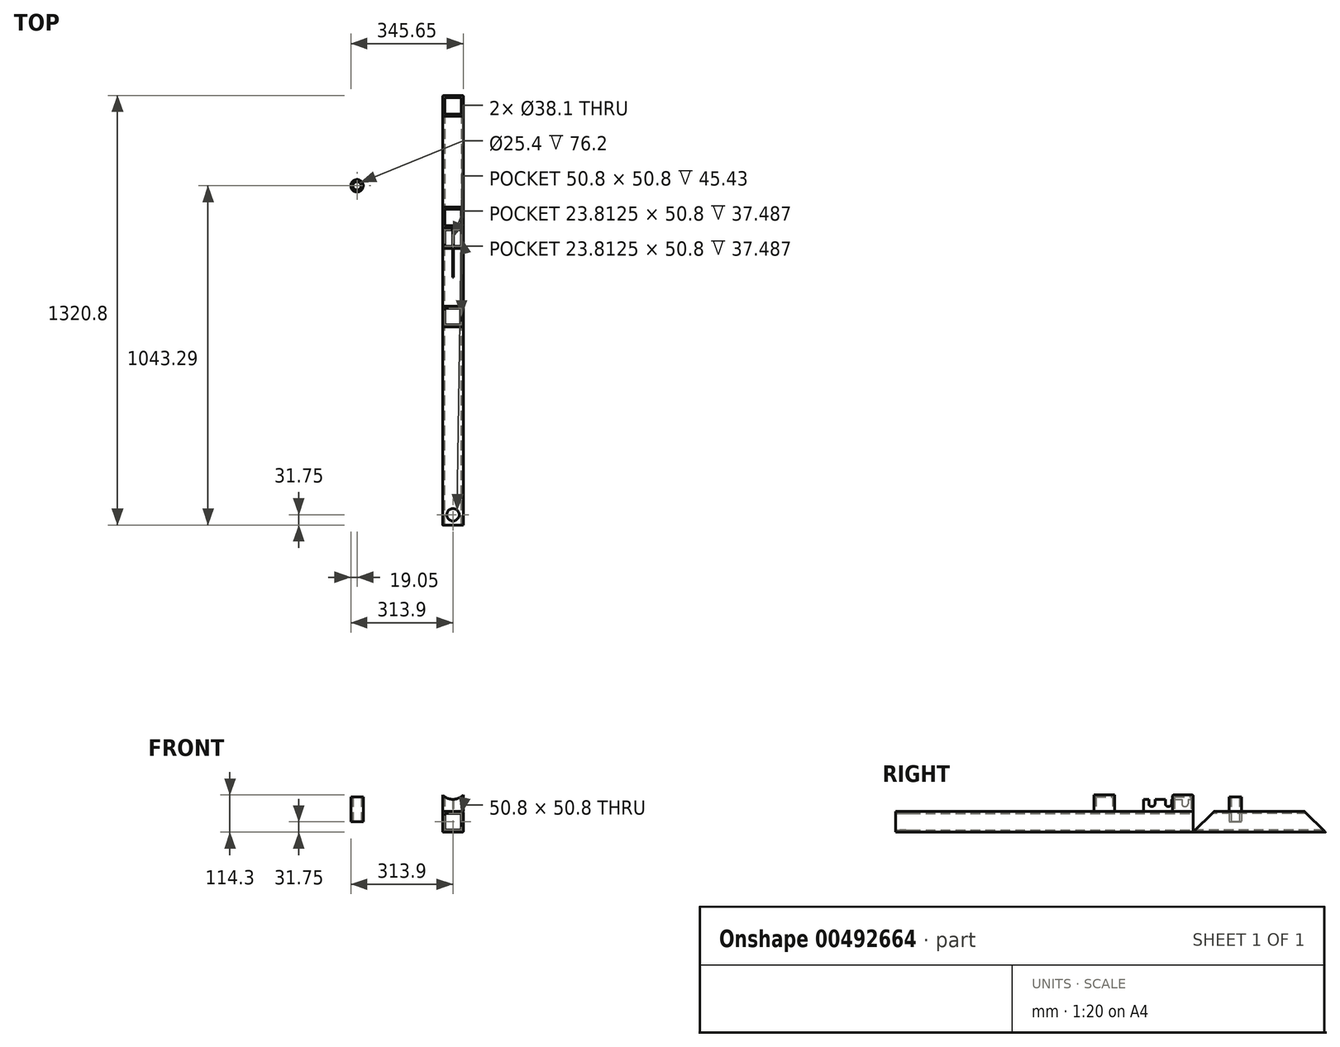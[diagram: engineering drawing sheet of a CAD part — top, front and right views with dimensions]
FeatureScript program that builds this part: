
annotation { "Feature Type Name" : "Feature", "Feature Type Description" : "" }
export const myFeature = defineFeature(function(context is Context, id is Id, definition is map)
    precondition{}
    {
        {
            var Q0;
            Q0=qCreatedBy(makeId("Front.planeOp"),FACE);
            var sketch = newSketch(context, id + "F0", { "sketchPlane" : qUnion([Q0])});
            skLineSegment(sketch, "E0.bottom", {"start": v(28.75, -31.75) * mm, "end": v(-28.75, -31.75) * mm});
            skLineSegment(sketch, "E0.top", {"start": v(28.75, 31.75) * mm, "end": v(-28.75, 31.75) * mm});
            skLineSegment(sketch, "E0.left", {"start": v(31.75, -28.75) * mm, "end": v(31.75, 28.75) * mm});
            skLineSegment(sketch, "E0.right", {"start": v(-31.75, -28.75) * mm, "end": v(-31.75, 28.75) * mm});
            skPoint(sketch, "E0.middle", {"position": v(0, 0) * mm});
            skLineSegment(sketch, "E1.bottom", {"start": v(25.4, -25.4) * mm, "end": v(-25.4, -25.4) * mm});
            skLineSegment(sketch, "E1.top", {"start": v(25.4, 25.4) * mm, "end": v(-25.4, 25.4) * mm});
            skLineSegment(sketch, "E1.left", {"start": v(25.4, -25.4) * mm, "end": v(25.4, 25.4) * mm});
            skLineSegment(sketch, "E1.right", {"start": v(-25.4, -25.4) * mm, "end": v(-25.4, 25.4) * mm});
            skPoint(sketch, "E2.visualSharp", {"position": v(-31.75, 31.75) * mm});
            skArc(sketch, "E2.filletArc", {"start": v(-28.75, 31.75) * mm, "mid": v(-30.87, 30.87) * mm, "end": v(-31.75, 28.75) * mm});
            skPoint(sketch, "E3.visualSharp", {"position": v(31.75, 31.75) * mm});
            skArc(sketch, "E3.filletArc", {"start": v(31.75, 28.75) * mm, "mid": v(30.87, 30.87) * mm, "end": v(28.75, 31.75) * mm});
            skPoint(sketch, "E4.visualSharp", {"position": v(31.75, -31.75) * mm});
            skArc(sketch, "E4.filletArc", {"start": v(28.75, -31.75) * mm, "mid": v(30.87, -30.87) * mm, "end": v(31.75, -28.75) * mm});
            skPoint(sketch, "E5.visualSharp", {"position": v(-31.75, -31.75) * mm});
            skArc(sketch, "E5.filletArc", {"start": v(-31.75, -28.75) * mm, "mid": v(-30.87, -30.87) * mm, "end": v(-28.75, -31.75) * mm});
            skSolve(sketch);
        }
        {
            var Q0;
            Q0 = qSketchRegion(id + "F0", true);
            extrude(context, id + "F1", {"entities" : qUnion([Q0]), "depth" : 609.6 * mm, "offsetDistance" : 25 * mm});
        }
        {
            var Q0;
            Q0 = qSketchRegion(id + "F0", true);
            extrude(context, id + "F2", {"entities" : qUnion([Q0]), "depth" : 304.8 * mm, "offsetDistance" : 25 * mm});
        }
        {
            var Q0;
            Q0 = qSketchRegion(id + "F0", true);
            extrude(context, id + "F3", {"entities" : qUnion([Q0]), "oppositeDirection" : true, "depth" : 406.4 * mm, "offsetDistance" : 25 * mm});
        }
        {
            var Q0;
            Q0=makeQuery(id+"F3.opExtrude","SWEPT_FACE",FACE,{"disambiguationData":[OSD([sQuery(id+"F0.wireOp",EDGE,"E0.right")])]});
            var sketch = newSketch(context, id + "F4", { "sketchPlane" : qUnion([Q0])});
            skPoint(sketch, "E6.middle", {"position": v(-374.65, 0) * mm});
            skPoint(sketch, "E6.middle.positionSnap0", {"position": v(-406.4, 0) * mm});
            skPoint(sketch, "E6.centerSnap0", {"position": v(-406.4, 0) * mm});
            skLineSegment(sketch, "E7", {"start": v(-406.4, -28.75) * mm, "end": v(-406.4, 28.75) * mm});
            skLineSegment(sketch, "E8", {"start": v(-342.9, 31.75) * mm, "end": v(-406.4, 31.75) * mm});
            skLineSegment(sketch, "E9", {"start": v(-342.9, 31.75) * mm, "end": v(-406.4, -31.75) * mm});
            skLineSegment(sketch, "E10", {"start": v(-406.4, 31.75) * mm, "end": v(-406.4, -31.75) * mm});
            skSolve(sketch);
        }
        {
            var Q0;
            Q0 = qSketchRegion(id + "F4", true);
            extrude(context, id + "F5", {"entities" : qUnion([Q0]), "operationType" : NewBodyOperationType.REMOVE, "endBound" : BoundingType.THROUGH_ALL, "oppositeDirection" : true, "depth" : 25 * mm, "offsetDistance" : 25 * mm});
        }
        {
            var Q0;
            Q0=makeQuery(id+"F3.opExtrude","SWEPT_FACE",FACE,{"disambiguationData":[OSD([sQuery(id+"F0.wireOp",EDGE,"E0.right")])]});
            var sketch = newSketch(context, id + "F6", { "sketchPlane" : qUnion([Q0])});
            skPoint(sketch, "E11.middle", {"position": v(-31.75, 0) * mm});
            skLineSegment(sketch, "E12", {"start": v(-63.5, 31.75) * mm, "end": v(0, -31.75) * mm});
            skLineSegment(sketch, "E13", {"start": v(0, 31.75) * mm, "end": v(0, -31.75) * mm});
            skLineSegment(sketch, "E14", {"start": v(0, 31.75) * mm, "end": v(-63.5, 31.75) * mm});
            skSolve(sketch);
        }
        {
            var Q0;
            Q0 = qSketchRegion(id + "F6", true);
            extrude(context, id + "F7", {"entities" : qUnion([Q0]), "operationType" : NewBodyOperationType.REMOVE, "endBound" : BoundingType.THROUGH_ALL, "oppositeDirection" : true, "depth" : 25 * mm, "offsetDistance" : 25 * mm});
        }
        {
            var Q0;
            Q0=makeQuery(id+"F1.opExtrude","SWEPT_FACE",FACE,{"disambiguationData":[OSD([sQuery(id+"F0.wireOp",EDGE,"E0.top")])]});
            var sketch = newSketch(context, id + "F8", { "sketchPlane" : qUnion([Q0])});
            skPoint(sketch, "E15.centerSnap0", {"position": v(0, -609.6) * mm});
            skCircle(sketch, "E16", {"center": v(0, -577.85) * mm, "radius": 19.05 * mm});
            skSolve(sketch);
        }
        {
            var Q0;
            Q0 = qSketchRegion(id + "F8", true);
            extrude(context, id + "F9", {"entities" : qUnion([Q0]), "operationType" : NewBodyOperationType.REMOVE, "endBound" : BoundingType.THROUGH_ALL, "oppositeDirection" : true, "depth" : 25.4 * mm, "offsetDistance" : 25 * mm});
        }
        {
            var Q0;
            Q0=qCreatedBy(makeId("Front.planeOp"),FACE);
            var sketch = newSketch(context, id + "F10", { "sketchPlane" : qUnion([Q0])});
            skLineSegment(sketch, "E17.bottom", {"start": v(-25.4, -25.4) * mm, "end": v(25.4, -25.4) * mm});
            skLineSegment(sketch, "E17.top", {"start": v(-25.4, 25.4) * mm, "end": v(25.4, 25.4) * mm});
            skLineSegment(sketch, "E17.left", {"start": v(-25.4, -25.4) * mm, "end": v(-25.4, 25.4) * mm});
            skLineSegment(sketch, "E17.right", {"start": v(25.4, -25.4) * mm, "end": v(25.4, 25.4) * mm});
            skPoint(sketch, "E17.middle", {"position": v(0, 0) * mm});
            skLineSegment(sketch, "E18.bottom", {"start": v(-28.75, -31.75) * mm, "end": v(28.75, -31.75) * mm});
            skLineSegment(sketch, "E18.top", {"start": v(-28.75, 31.75) * mm, "end": v(28.75, 31.75) * mm});
            skLineSegment(sketch, "E18.left", {"start": v(-31.75, -28.75) * mm, "end": v(-31.75, 28.75) * mm});
            skLineSegment(sketch, "E18.right", {"start": v(31.75, -28.75) * mm, "end": v(31.75, 28.75) * mm});
            skPoint(sketch, "E19.visualSharp", {"position": v(31.75, 31.75) * mm});
            skArc(sketch, "E19.filletArc", {"start": v(31.75, 28.75) * mm, "mid": v(30.87, 30.87) * mm, "end": v(28.75, 31.75) * mm});
            skPoint(sketch, "E20.visualSharp", {"position": v(-31.75, 31.75) * mm});
            skArc(sketch, "E20.filletArc", {"start": v(-28.75, 31.75) * mm, "mid": v(-30.87, 30.87) * mm, "end": v(-31.75, 28.75) * mm});
            skPoint(sketch, "E21.visualSharp", {"position": v(-31.75, -31.75) * mm});
            skArc(sketch, "E21.filletArc", {"start": v(-31.75, -28.75) * mm, "mid": v(-30.87, -30.87) * mm, "end": v(-28.75, -31.75) * mm});
            skPoint(sketch, "E22.visualSharp", {"position": v(31.75, -31.75) * mm});
            skArc(sketch, "E22.filletArc", {"start": v(28.75, -31.75) * mm, "mid": v(30.87, -30.87) * mm, "end": v(31.75, -28.75) * mm});
            skSolve(sketch);
        }
        {
            var Q0;
            Q0 = qSketchRegion(id + "F10", true);
            extrude(context, id + "F11", {"entities" : qUnion([Q0]), "depth" : 914.4 * mm, "offsetDistance" : 25 * mm});
        }
        {
            var Q0;
            Q0=makeQuery(id+"F11.opExtrude","SWEPT_FACE",FACE,{"disambiguationData":[OSD([sQuery(id+"F10.wireOp",EDGE,"E18.bottom")])]});
            var sketch = newSketch(context, id + "F12", { "sketchPlane" : qUnion([Q0])});
            skCircle(sketch, "E23", {"center": v(0, 882.65) * mm, "radius": 19.05 * mm});
            skPoint(sketch, "E23.centerSnap0", {"position": v(0, 914.4) * mm});
            skSolve(sketch);
        }
        {
            var Q0;
            Q0 = qSketchRegion(id + "F12", true);
            extrude(context, id + "F13", {"entities" : qUnion([Q0]), "operationType" : NewBodyOperationType.REMOVE, "endBound" : BoundingType.THROUGH_ALL, "oppositeDirection" : true, "depth" : 25.4 * mm, "offsetDistance" : 25 * mm});
        }
        {
            var Q0;
            Q0=makeQuery(id+"F11.opExtrude","SWEPT_FACE",FACE,{"disambiguationData":[OSD([sQuery(id+"F10.wireOp",EDGE,"E18.top")])]});
            var sketch = newSketch(context, id + "F14", { "sketchPlane" : qUnion([Q0])});
            skLineSegment(sketch, "E24.bottom", {"start": v(-1.59, 0) * mm, "end": v(1.59, 0) * mm});
            skLineSegment(sketch, "E24.top", {"start": v(-1.59, -152.4) * mm, "end": v(1.59, -152.4) * mm});
            skLineSegment(sketch, "E24.left", {"start": v(-1.59, 0) * mm, "end": v(-1.59, -152.4) * mm});
            skLineSegment(sketch, "E24.right", {"start": v(1.59, 0) * mm, "end": v(1.59, -152.4) * mm});
            skPoint(sketch, "E24.middle", {"position": v(0, -76.2) * mm});
            skSolve(sketch);
        }
        {
            var Q0;
            Q0 = qSketchRegion(id + "F14", true);
            extrude(context, id + "F15", {"entities" : qUnion([Q0]), "operationType" : NewBodyOperationType.ADD, "depth" : 76.2 * mm, "offsetDistance" : 25 * mm});
        }
        {
            var Q0;
            Q0=makeQuery(id+"F15.opExtrude","SWEPT_FACE",FACE,{"disambiguationData":[OSD([sQuery(id+"F14.wireOp",EDGE,"E24.right")])]});
            var sketch = newSketch(context, id + "F16", { "sketchPlane" : qUnion([Q0])});
            skLineSegment(sketch, "E25", {"start": v(-152.4, 101.6) * mm, "end": v(0, 101.6) * mm, "construction": true});
            skCircle(sketch, "E26", {"center": v(-127, 85.72) * mm, "radius": 15.88 * mm});
            skLineSegment(sketch, "E27", {"start": v(-76.2, 101.6) * mm, "end": v(-76.2, 52.57) * mm, "construction": true});
            skLineSegment(sketch, "E28.bottom", {"start": v(-136.53, 73.02) * mm, "end": v(-117.48, 73.02) * mm});
            skLineSegment(sketch, "E28.top", {"start": v(-128.53, 47.62) * mm, "end": v(-125.48, 47.62) * mm});
            skLineSegment(sketch, "E28.left", {"start": v(-136.53, 73.02) * mm, "end": v(-136.53, 55.62) * mm});
            skLineSegment(sketch, "E28.right", {"start": v(-117.48, 73.02) * mm, "end": v(-117.48, 55.62) * mm});
            skPoint(sketch, "E28.middle", {"position": v(-127, 60.32) * mm});
            skPoint(sketch, "E29.visualSharp", {"position": v(-136.53, 47.62) * mm});
            skArc(sketch, "E29.filletArc", {"start": v(-136.53, 55.62) * mm, "mid": v(-134.18, 49.97) * mm, "end": v(-128.53, 47.62) * mm});
            skPoint(sketch, "E30.visualSharp", {"position": v(-117.48, 47.62) * mm});
            skArc(sketch, "E30.filletArc", {"start": v(-125.48, 47.62) * mm, "mid": v(-119.82, 49.97) * mm, "end": v(-117.47, 55.62) * mm});
            skCircle(sketch, "E31.1.0.0", {"center": v(-76.2, 85.72) * mm, "radius": 15.88 * mm});
            skLineSegment(sketch, "E31.1.0.1", {"start": v(-66.67, 73.02) * mm, "end": v(-66.67, 55.62) * mm});
            skLineSegment(sketch, "E31.1.0.2", {"start": v(-85.72, 73.02) * mm, "end": v(-85.72, 55.62) * mm});
            skLineSegment(sketch, "E31.1.0.3", {"start": v(-85.72, 73.02) * mm, "end": v(-66.67, 73.02) * mm});
            skArc(sketch, "E31.1.0.4", {"start": v(-74.67, 47.62) * mm, "mid": v(-69.02, 49.97) * mm, "end": v(-66.67, 55.62) * mm});
            skLineSegment(sketch, "E31.1.0.5", {"start": v(-77.72, 47.62) * mm, "end": v(-74.67, 47.62) * mm});
            skArc(sketch, "E31.1.0.6", {"start": v(-85.72, 55.62) * mm, "mid": v(-83.38, 49.97) * mm, "end": v(-77.72, 47.62) * mm});
            skCircle(sketch, "E31.2.0.0", {"center": v(-25.4, 85.72) * mm, "radius": 15.88 * mm});
            skLineSegment(sketch, "E31.2.0.1", {"start": v(-15.87, 73.02) * mm, "end": v(-15.87, 55.62) * mm});
            skLineSegment(sketch, "E31.2.0.2", {"start": v(-34.92, 73.02) * mm, "end": v(-34.92, 55.62) * mm});
            skLineSegment(sketch, "E31.2.0.3", {"start": v(-34.92, 73.02) * mm, "end": v(-15.87, 73.02) * mm});
            skArc(sketch, "E31.2.0.4", {"start": v(-23.87, 47.62) * mm, "mid": v(-18.22, 49.97) * mm, "end": v(-15.87, 55.62) * mm});
            skLineSegment(sketch, "E31.2.0.5", {"start": v(-26.92, 47.62) * mm, "end": v(-23.87, 47.62) * mm});
            skArc(sketch, "E31.2.0.6", {"start": v(-34.92, 55.62) * mm, "mid": v(-32.58, 49.97) * mm, "end": v(-26.92, 47.62) * mm});
            skLineSegment(sketch, "E31.direction1", {"start": v(-127, 85.72) * mm, "end": v(-76.2, 85.72) * mm, "construction": true});
            skSolve(sketch);
        }
        {
            var Q0;
            Q0 = qSketchRegion(id + "F16", true);
            extrude(context, id + "F17", {"entities" : qUnion([Q0]), "operationType" : NewBodyOperationType.REMOVE, "endBound" : BoundingType.THROUGH_ALL, "oppositeDirection" : true, "depth" : 25 * mm, "offsetDistance" : 25 * mm});
        }
        {
            var Q0;
            Q0=makeQuery(id+"F2.opExtrude","SWEPT_FACE",FACE,{"disambiguationData":[OSD([sQuery(id+"F0.wireOp",EDGE,"E0.top")])]});
            var sketch = newSketch(context, id + "F18", { "sketchPlane" : qUnion([Q0])});
            skLineSegment(sketch, "E32.bottom", {"start": v(-28.75, 0) * mm, "end": v(28.75, 0) * mm});
            skLineSegment(sketch, "E32.top", {"start": v(-28.75, -63.5) * mm, "end": v(28.75, -63.5) * mm});
            skLineSegment(sketch, "E32.left", {"start": v(-31.75, -3) * mm, "end": v(-31.75, -60.5) * mm});
            skLineSegment(sketch, "E32.right", {"start": v(31.75, -3) * mm, "end": v(31.75, -60.5) * mm});
            skPoint(sketch, "E32.middle", {"position": v(0, -31.75) * mm});
            skLineSegment(sketch, "E33.bottom", {"start": v(25.4, -57.15) * mm, "end": v(-25.4, -57.15) * mm});
            skLineSegment(sketch, "E33.top", {"start": v(25.4, -6.35) * mm, "end": v(-25.4, -6.35) * mm});
            skLineSegment(sketch, "E33.left", {"start": v(25.4, -57.15) * mm, "end": v(25.4, -6.35) * mm});
            skLineSegment(sketch, "E33.right", {"start": v(-25.4, -57.15) * mm, "end": v(-25.4, -6.35) * mm});
            skLineSegment(sketch, "E34", {"start": v(-28.75, -152.4) * mm, "end": v(28.75, -152.4) * mm, "construction": true});
            skLineSegment(sketch, "E35.MirrorCS", {"start": v(25.4, -298.45) * mm, "end": v(-25.4, -298.45) * mm});
            skLineSegment(sketch, "E36.MirrorCS", {"start": v(-31.75, -304.8) * mm, "end": v(31.75, -304.8) * mm});
            skLineSegment(sketch, "E37.MirrorCS", {"start": v(-31.75, -304.8) * mm, "end": v(-31.75, -241.3) * mm});
            skLineSegment(sketch, "E38.MirrorCS", {"start": v(-25.4, -247.65) * mm, "end": v(-25.4, -298.45) * mm});
            skLineSegment(sketch, "E39.MirrorCS", {"start": v(25.4, -247.65) * mm, "end": v(-25.4, -247.65) * mm});
            skLineSegment(sketch, "E40.MirrorCS", {"start": v(-31.75, -241.3) * mm, "end": v(31.75, -241.3) * mm});
            skLineSegment(sketch, "E41.MirrorCS", {"start": v(25.4, -247.65) * mm, "end": v(25.4, -298.45) * mm});
            skLineSegment(sketch, "E42.MirrorCS", {"start": v(31.75, -304.8) * mm, "end": v(31.75, -241.3) * mm});
            skPoint(sketch, "E43.visualSharp", {"position": v(-31.75, 0) * mm});
            skArc(sketch, "E43.filletArc", {"start": v(-28.75, 0) * mm, "mid": v(-30.87, -0.88) * mm, "end": v(-31.75, -3) * mm});
            skPoint(sketch, "E44.visualSharp", {"position": v(-31.75, -63.5) * mm});
            skArc(sketch, "E44.filletArc", {"start": v(-31.75, -60.5) * mm, "mid": v(-30.87, -62.62) * mm, "end": v(-28.75, -63.5) * mm});
            skPoint(sketch, "E45.visualSharp", {"position": v(31.75, -63.5) * mm});
            skArc(sketch, "E45.filletArc", {"start": v(28.75, -63.5) * mm, "mid": v(30.87, -62.62) * mm, "end": v(31.75, -60.5) * mm});
            skPoint(sketch, "E46.visualSharp", {"position": v(31.75, 0) * mm});
            skArc(sketch, "E46.filletArc", {"start": v(31.75, -3) * mm, "mid": v(30.87, -0.88) * mm, "end": v(28.75, 0) * mm});
            skSolve(sketch);
        }
        {
            var Q0;
            Q0 = qSketchRegion(id + "F18", true);
            extrude(context, id + "F19", {"entities" : qUnion([Q0]), "operationType" : NewBodyOperationType.ADD, "depth" : 50.8 * mm, "offsetDistance" : 25 * mm});
        }
        {
            var Q0;
            Q0=makeQuery(id+"F19.boolean.opBoolean","MERGE",FACE,{"derivedFrom":[makeQuery(id+"F2.opExtrude","CAP_FACE",FACE,{"disambiguationData":[OSD([sQuery(id+"F0.wireOp",EDGE,"E0.bottom"),sQuery(id+"F0.wireOp",EDGE,"E0.top"),sQuery(id+"F0.wireOp",EDGE,"E0.left"),sQuery(id+"F0.wireOp",EDGE,"E0.right"),sQuery(id+"F0.wireOp",EDGE,"E1.bottom"),sQuery(id+"F0.wireOp",EDGE,"E1.top"),sQuery(id+"F0.wireOp",EDGE,"E1.left"),sQuery(id+"F0.wireOp",EDGE,"E1.right"),sQuery(id+"F0.wireOp",EDGE,"E2.filletArc"),sQuery(id+"F0.wireOp",EDGE,"E3.filletArc"),sQuery(id+"F0.wireOp",EDGE,"E4.filletArc"),sQuery(id+"F0.wireOp",EDGE,"E5.filletArc")])],"isStart":true}),makeQuery(id+"F19.opExtrude","SWEPT_FACE",FACE,{"disambiguationData":[OSD([sQuery(id+"F18.wireOp",EDGE,"E32.bottom")])]})]});
            var sketch = newSketch(context, id + "F20", { "sketchPlane" : qUnion([Q0])});
            skCircle(sketch, "E47", {"center": v(0, 113.66) * mm, "radius": 44.45 * mm});
            skSolve(sketch);
        }
        {
            var Q0;
            Q0 = qSketchRegion(id + "F20", true);
            extrude(context, id + "F21", {"entities" : qUnion([Q0]), "operationType" : NewBodyOperationType.REMOVE, "endBound" : BoundingType.THROUGH_ALL, "oppositeDirection" : true, "depth" : 25 * mm, "offsetDistance" : 25 * mm});
        }
        {
            var Q0;
            Q0=qCreatedBy(makeId("Top.planeOp"),FACE);
            var sketch = newSketch(context, id + "F22", { "sketchPlane" : qUnion([Q0])});
            skCircle(sketch, "E48", {"center": v(-294.85, 128.9) * mm, "radius": 19.05 * mm});
            skCircle(sketch, "E49", {"center": v(-294.85, 128.9) * mm, "radius": 12.7 * mm});
            skSolve(sketch);
        }
        {
            var Q0;
            Q0 = qSketchRegion(id + "F22", true);
            extrude(context, id + "F23", {"entities" : qUnion([Q0]), "depth" : 76.2 * mm, "offsetDistance" : 25 * mm});
        }
    });
